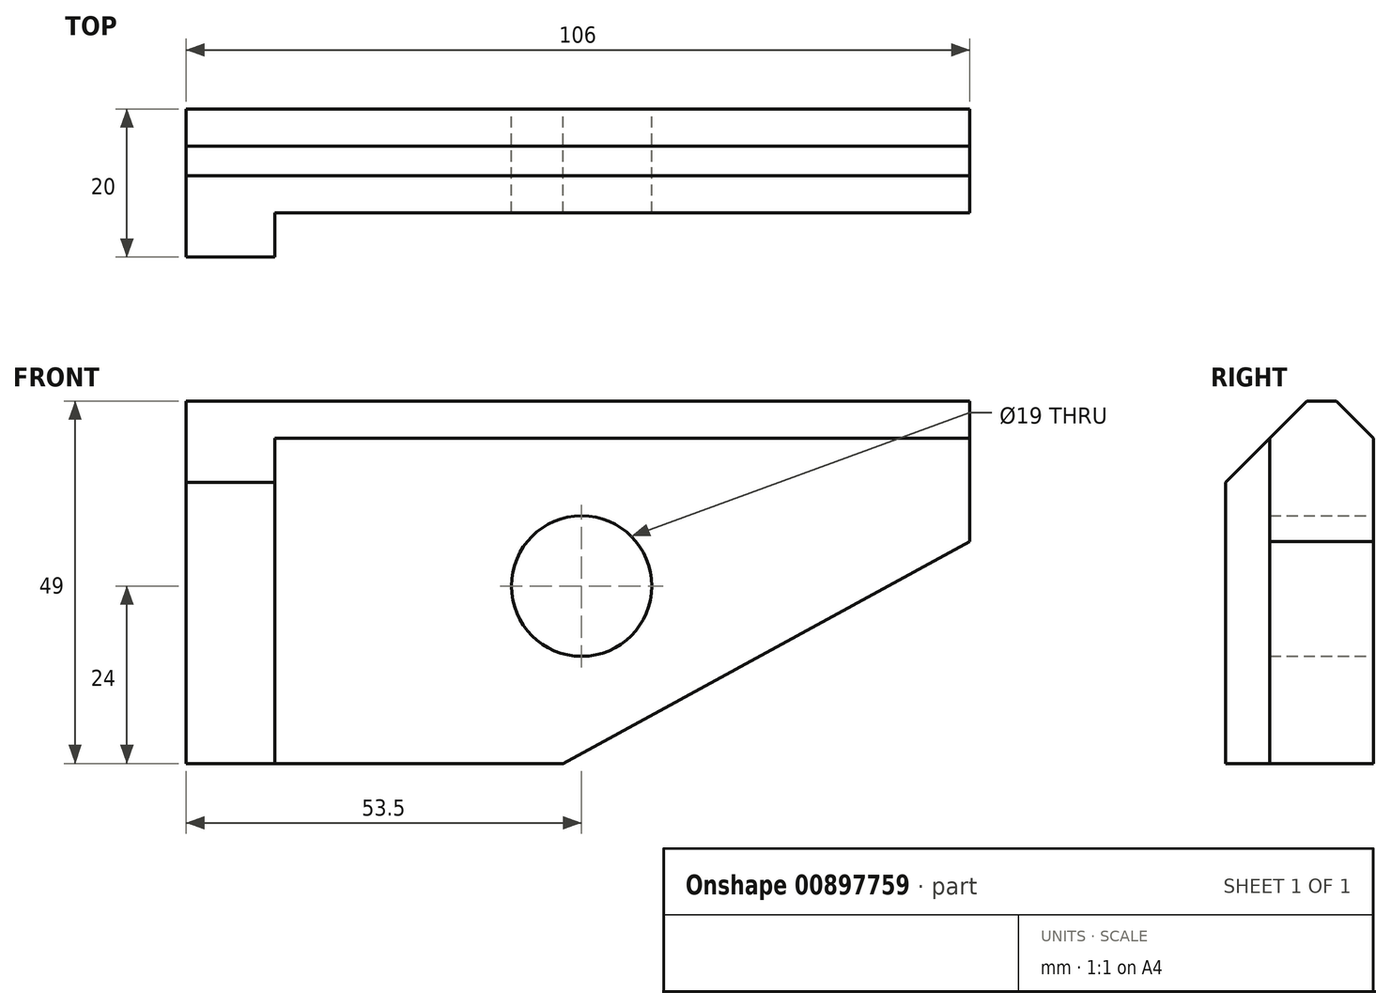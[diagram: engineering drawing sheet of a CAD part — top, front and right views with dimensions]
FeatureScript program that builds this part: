
annotation { "Feature Type Name" : "Feature", "Feature Type Description" : "" }
export const myFeature = defineFeature(function(context is Context, id is Id, definition is map)
    precondition{}
    {
        {
            var Q0;
            Q0=qCreatedBy(makeId("Front.planeOp"),FACE);
            var sketch = newSketch(context, id + "F0", { "sketchPlane" : qUnion([Q0])});
            skLineSegment(sketch, "E0", {"start": v(-53.5, 25) * mm, "end": v(52.5, 25) * mm});
            skLineSegment(sketch, "E1", {"start": v(-53.5, 25) * mm, "end": v(-53.5, -24) * mm});
            skLineSegment(sketch, "E2", {"start": v(-53.5, -24) * mm, "end": v(-2.5, -24) * mm});
            skLineSegment(sketch, "E3", {"start": v(-2.5, -24) * mm, "end": v(52.5, 6) * mm});
            skLineSegment(sketch, "E4", {"start": v(52.5, 6) * mm, "end": v(52.5, 25) * mm});
            skCircle(sketch, "E5", {"center": v(0, 0) * mm, "radius": 9.5 * mm});
            skSolve(sketch);
        }
        {
            var Q0;
            Q0 = qSketchRegion(id + "F0", true);
            extrude(context, id + "F1", {"entities" : qUnion([Q0]), "depth" : 14 * mm, "offsetDistance" : 25 * mm});
        }
        {
            var Q0;
            Q0=makeQuery(id+"F1.opExtrude","CAP_FACE",FACE,{"disambiguationData":[OSD([sQuery(id+"F0.wireOp",EDGE,"E0"),sQuery(id+"F0.wireOp",EDGE,"E1"),sQuery(id+"F0.wireOp",EDGE,"E2"),sQuery(id+"F0.wireOp",EDGE,"E3"),sQuery(id+"F0.wireOp",EDGE,"E4"),sQuery(id+"F0.wireOp",EDGE,"E5")])],"isStart":false});
            var sketch = newSketch(context, id + "F2", { "sketchPlane" : qUnion([Q0])});
            skLineSegment(sketch, "E6.bottom", {"start": v(-53.5, 25) * mm, "end": v(-41.5, 25) * mm});
            skLineSegment(sketch, "E6.top", {"start": v(-53.5, -24) * mm, "end": v(-41.5, -24) * mm});
            skLineSegment(sketch, "E6.left", {"start": v(-53.5, 25) * mm, "end": v(-53.5, -24) * mm});
            skLineSegment(sketch, "E6.right", {"start": v(-41.5, 25) * mm, "end": v(-41.5, -24) * mm});
            skSolve(sketch);
        }
        {
            var Q0;
            Q0 = qSketchRegion(id + "F2", true);
            extrude(context, id + "F3", {"entities" : qUnion([Q0]), "operationType" : NewBodyOperationType.ADD, "depth" : 6 * mm, "offsetDistance" : 25 * mm});
        }
        {
            var Q0;
            Q0=makeQuery(id+"F3.boolean.opBoolean","MERGE",FACE,{"derivedFrom":[makeQuery(id+"F1.opExtrude","SWEPT_FACE",FACE,{"disambiguationData":[OSD([sQuery(id+"F0.wireOp",EDGE,"E1")])]}),makeQuery(id+"F3.opExtrude","SWEPT_FACE",FACE,{"disambiguationData":[OSD([sQuery(id+"F2.wireOp",EDGE,"E6.left")])]})]});
            var sketch = newSketch(context, id + "F4", { "sketchPlane" : qUnion([Q0])});
            skLineSegment(sketch, "E7", {"start": v(0, 20) * mm, "end": v(5, 25) * mm});
            skLineSegment(sketch, "E8", {"start": v(5, 25) * mm, "end": v(0, 25) * mm});
            skLineSegment(sketch, "E9", {"start": v(0, 25) * mm, "end": v(0, 20) * mm});
            skLineSegment(sketch, "E10", {"start": v(9, 25) * mm, "end": v(20, 14) * mm});
            skLineSegment(sketch, "E11", {"start": v(20, 14) * mm, "end": v(20, 25) * mm});
            skLineSegment(sketch, "E12", {"start": v(20, 25) * mm, "end": v(9, 25) * mm});
            skLineSegment(sketch, "E13", {"start": v(14, 25) * mm, "end": v(14, 20) * mm, "construction": true});
            skSolve(sketch);
        }
        {
            var Q0;
            Q0=makeQuery(id+"F4.imprint","IMPRINT",FACE,{"disambiguationData":[TD([[makeQuery(id+"F4.imprint","IMPRINT",EDGE,{"derivedFrom":sQuery(id+"F4.wireOp",EDGE,"E10")}),1.0]])]});
            var Q1;
            Q1=makeQuery(id+"F4.imprint","IMPRINT",FACE,{"disambiguationData":[TD([[makeQuery(id+"F4.imprint","IMPRINT",EDGE,{"derivedFrom":sQuery(id+"F4.wireOp",EDGE,"E7")}),1.0]])]});
            extrude(context, id + "F5", {"entities" : qUnion([Q0, Q1]), "operationType" : NewBodyOperationType.REMOVE, "endBound" : BoundingType.UP_TO_NEXT, "oppositeDirection" : true, "depth" : 108.7 * mm, "offsetDistance" : 25 * mm});
        }
    });
